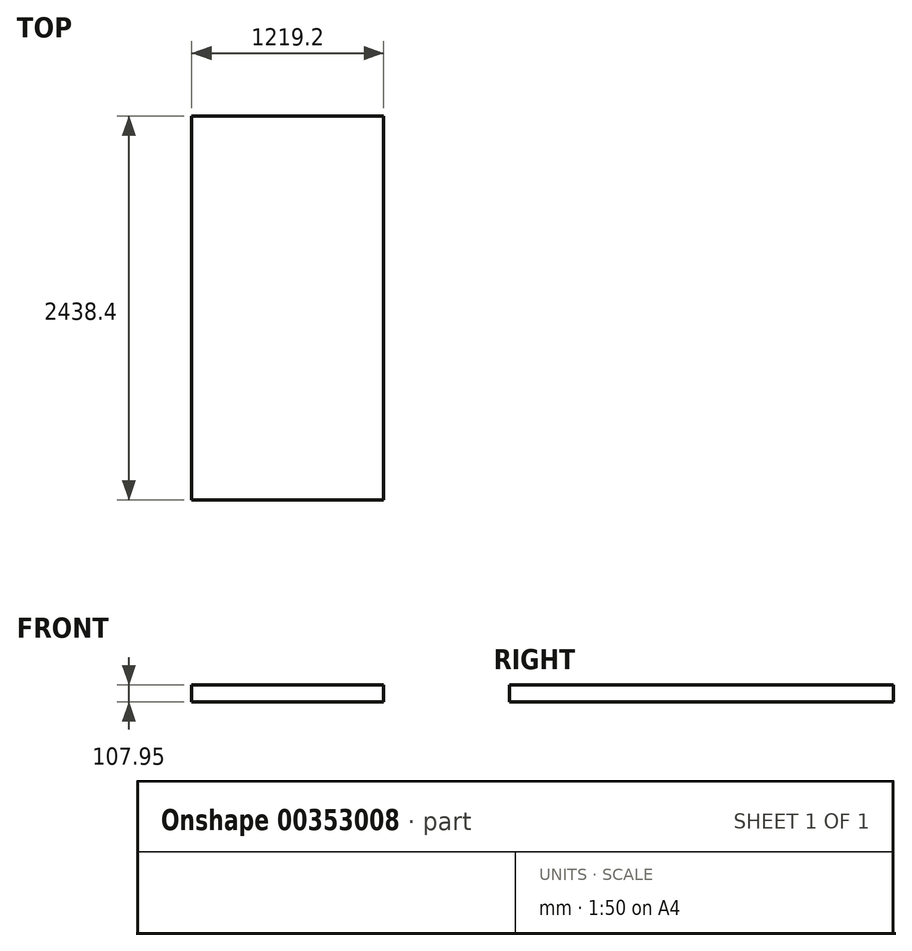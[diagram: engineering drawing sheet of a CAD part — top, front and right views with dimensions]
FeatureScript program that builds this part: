
annotation { "Feature Type Name" : "Feature", "Feature Type Description" : "" }
export const myFeature = defineFeature(function(context is Context, id is Id, definition is map)
    precondition{}
    {
        {
            var Q0;
            Q0=qCreatedBy(makeId("Top.planeOp"),FACE);
            var sketch = newSketch(context, id + "F0", { "sketchPlane" : qUnion([Q0])});
            skLineSegment(sketch, "E0.bottom", {"start": v(-612.41, 1253.38) * mm, "end": v(606.79, 1253.38) * mm});
            skLineSegment(sketch, "E0.top", {"start": v(-612.41, -1185.02) * mm, "end": v(606.79, -1185.02) * mm});
            skLineSegment(sketch, "E0.left", {"start": v(-612.41, 1253.38) * mm, "end": v(-612.41, -1185.02) * mm});
            skLineSegment(sketch, "E0.right", {"start": v(606.79, 1253.38) * mm, "end": v(606.79, -1185.02) * mm});
            skSolve(sketch);
        }
        {
            var Q0;
            Q0 = qSketchRegion(id + "F0", true);
            extrude(context, id + "F1", {"entities" : qUnion([Q0]), "depth" : 107.95 * mm});
        }
    });
